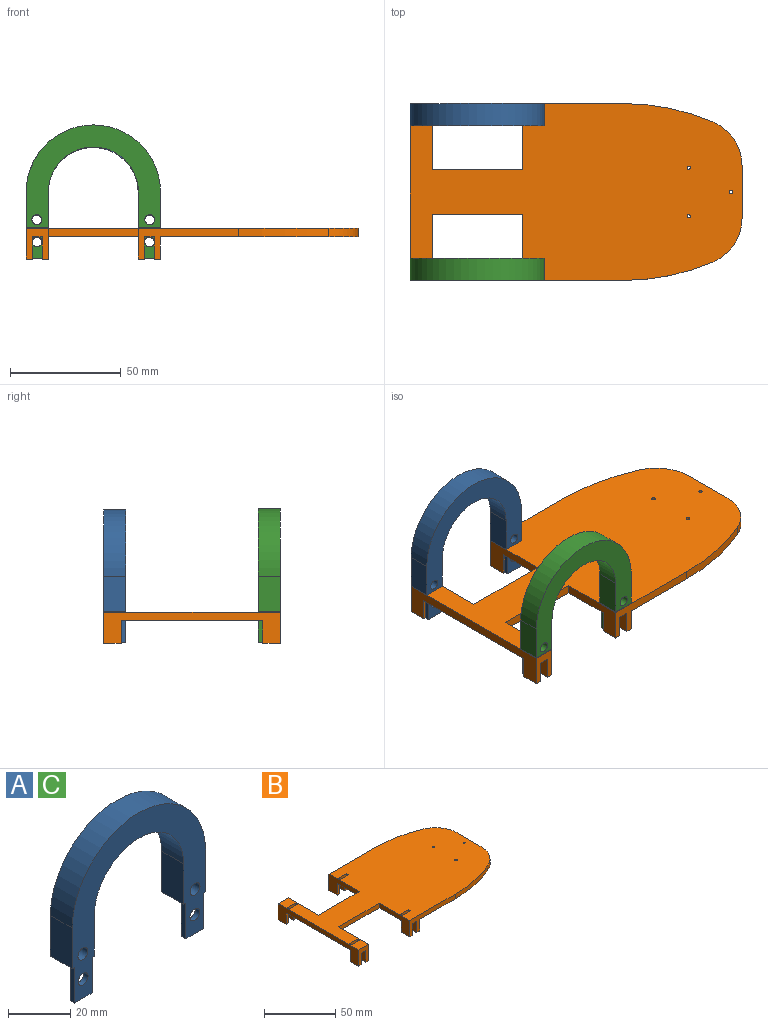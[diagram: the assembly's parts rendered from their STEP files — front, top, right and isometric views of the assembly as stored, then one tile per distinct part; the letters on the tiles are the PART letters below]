
ASSEMBLY  parts=3 mates=1
PART A: 22 faces, bbox 60.7x10x60.4 mm
  f0: plane 60.7x60.35mm, normal (0,-1,0), area 1276.8mm2, adj f2,f3,f4,f5,f6,f7,f8,f9
  f1: plane 60.7x46.35mm, normal (0,1,0), area 1084.6mm2, adj f2,f3,f4,f5,f6,f7,f8,f9
  f2: plane 10x10mm, normal (0,0,-1), area 84mm2, adj f0,f1,f5,f6,f14,f15,f16
  f3: plane 16x10mm, normal (1,0,0), area 160mm2, adj f0,f1,f4,f9
  f4: cylinder r=20.35mm len=40.7mm, axis (0,1,0), area 639.3mm2, adj f0,f1,f3,f5
  f5: plane 16x10mm, normal (-1,0,0), area 160mm2, adj f0,f1,f2,f4
  f6: plane 16x10mm, normal (1,0,0), area 160mm2, adj f0,f1,f2,f7
  f7: cylinder r=30.35mm len=60.7mm, axis (0,1,0), area 953.5mm2, adj f0,f1,f6,f8
  f8: plane 16x10mm, normal (-1,0,0), area 160mm2, adj f0,f1,f7,f9
  f9: plane 10x10mm, normal (0,0,-1), area 84mm2, adj f0,f1,f3,f8,f10,f11,f12
  f10: plane 14x2mm, normal (1,0,0), area 28mm2, adj f0,f9,f12,f13
  f11: plane 14x2mm, normal (-1,0,0), area 28mm2, adj f0,f9,f12,f13
  f12: plane 14x8mm, normal (0,1,0), area 96.1mm2, adj f9,f10,f11,f13,f19
  f13: plane 8x2mm, normal (0,0,-1), area 16mm2, adj f0,f10,f11,f12
  f14: plane 14x2mm, normal (-1,0,0), area 28mm2, adj f0,f2,f15,f17
  f15: plane 14x8mm, normal (0,1,0), area 96.1mm2, adj f2,f14,f16,f17,f18
  f16: plane 14x2mm, normal (1,0,0), area 28mm2, adj f0,f2,f15,f17
  f17: plane 8x2mm, normal (0,0,-1), area 16mm2, adj f0,f14,f15,f16
  f18: cylinder r=2.25mm len=4.5mm, axis (0,1,0), area 28.3mm2, adj f0,f15
  f19: cylinder r=2.25mm len=4.5mm, axis (0,1,0), area 28.3mm2, adj f0,f12
  f20: cylinder r=2.25mm len=10mm, axis (0,1,0), area 141.4mm2, adj f0,f1
  f21: cylinder r=2.25mm len=10mm, axis (0,1,0), area 141.4mm2, adj f0,f1
PART B: 59 faces, bbox 150x80x14 mm
  f0: plane 150x80mm, normal (0,0,-1), area 8584mm2, adj f6,f7,f8,f10,f12,f13,f14,f15
  f1: plane 150x80mm, normal (0,0,1), area 8904mm2, adj f6,f7,f8,f9,f10,f11,f12,f13
  f2: plane 8x4.5mm, normal (0,0,-1), area 36mm2, adj f7,f24,f48,f50
  f3: plane 8x4.5mm, normal (0,0,-1), area 36mm2, adj f9,f20,f43,f45
  f4: plane 8x4.5mm, normal (0,0,-1), area 36mm2, adj f8,f29,f38,f41
  f5: plane 8x4.5mm, normal (0,0,-1), area 36mm2, adj f11,f32,f34,f36
  f6: plane 23.72x4mm, normal (1,0,0), area 94.9mm2, adj f0,f1,f54,f55
  f7: plane 45.39x14mm, normal (0,1,0), area 236.6mm2, adj f0,f1,f2,f17,f47,f48,f49,f50
  f8: plane 45.39x14mm, normal (0,-1,0), area 236.6mm2, adj f0,f1,f4,f13,f38,f39,f40,f41
  f9: plane 14x10mm, normal (0,1,0), area 95mm2, adj f1,f3,f10,f15,f43,f44,f45,f46
  f10: plane 80x14mm, normal (-1,0,0), area 480mm2, adj f0,f1,f9,f11,f20,f32,f35,f44
  f11: plane 14x10mm, normal (0,-1,0), area 95mm2, adj f1,f5,f10,f12,f34,f35,f36,f37
  f12: plane 30x14mm, normal (1,0,0), area 200mm2, adj f0,f1,f11,f14,f32,f37
  f13: plane 30x14mm, normal (-1,0,0), area 200mm2, adj f0,f1,f8,f14,f29,f39
  f14: plane 40.7x4mm, normal (0,-1,0), area 162.8mm2, adj f0,f1,f12,f13
  f15: plane 30x14mm, normal (1,0,0), area 200mm2, adj f0,f1,f9,f16,f20,f46
  f16: plane 40.7x4mm, normal (0,1,0), area 162.8mm2, adj f0,f1,f15,f17
  f17: plane 30x14mm, normal (-1,0,0), area 200mm2, adj f0,f1,f7,f16,f24,f51
  f18: plane 8x4mm, normal (0,1,0), area 32mm2, adj f0,f1,f19,f21
  f19: plane 4x2mm, normal (-1,0,0), area 8mm2, adj f0,f1,f18,f20
  f20: plane 14x10mm, normal (0,-1,0), area 87mm2, adj f0,f1,f3,f10,f15,f19,f21,f43
  f21: plane 4x2mm, normal (1,0,0), area 8mm2, adj f0,f1,f18,f20
  f22: plane 8x4mm, normal (0,1,0), area 32mm2, adj f0,f1,f23,f25
  f23: plane 4x2mm, normal (-1,0,0), area 8mm2, adj f0,f1,f22,f24
  f24: plane 14x10mm, normal (0,-1,0), area 87mm2, adj f0,f1,f2,f17,f23,f25,f47,f48
  f25: plane 4x2mm, normal (1,0,0), area 8mm2, adj f0,f1,f22,f24
  f26: plane 4x2mm, normal (-1,0,0), area 8mm2, adj f0,f1,f27,f29
  f27: plane 8x4mm, normal (0,-1,0), area 32mm2, adj f0,f1,f26,f28
  f28: plane 4x2mm, normal (1,0,0), area 8mm2, adj f0,f1,f27,f29
  f29: plane 14x10mm, normal (0,1,0), area 87mm2, adj f0,f1,f4,f13,f26,f28,f38,f39
  f30: plane 8x4mm, normal (0,-1,0), area 32mm2, adj f0,f1,f31,f33
  f31: plane 4x2mm, normal (1,0,0), area 8mm2, adj f0,f1,f30,f32
  f32: plane 14x10mm, normal (0,1,0), area 87mm2, adj f0,f1,f5,f10,f12,f31,f33,f34
  f33: plane 4x2mm, normal (-1,0,0), area 8mm2, adj f0,f1,f30,f32
  f34: plane 10x8mm, normal (1,0,0), area 80mm2, adj f5,f11,f32,f35
  f35: plane 8x2.75mm, normal (0,0,-1), area 22mm2, adj f10,f11,f32,f34
  f36: plane 10x8mm, normal (-1,0,0), area 80mm2, adj f5,f11,f32,f37
  f37: plane 8x2.75mm, normal (0,0,-1), area 22mm2, adj f11,f12,f32,f36
  f38: plane 10x8mm, normal (1,0,0), area 80mm2, adj f4,f8,f29,f39
  f39: plane 8x2.75mm, normal (0,0,-1), area 22mm2, adj f8,f13,f29,f38
  f40: plane 10x8mm, normal (1,0,0), area 80mm2, adj f0,f8,f29,f42
  f41: plane 10x8mm, normal (-1,0,0), area 80mm2, adj f4,f8,f29,f42
  f42: plane 8x2.75mm, normal (0,0,-1), area 22mm2, adj f8,f29,f40,f41
  f43: plane 10x8mm, normal (1,0,0), area 80mm2, adj f3,f9,f20,f44
  f44: plane 8x2.75mm, normal (0,0,-1), area 22mm2, adj f9,f10,f20,f43
  f45: plane 10x8mm, normal (-1,0,0), area 80mm2, adj f3,f9,f20,f46
  f46: plane 8x2.75mm, normal (0,0,-1), area 22mm2, adj f9,f15,f20,f45
  f47: plane 10x8mm, normal (1,0,0), area 80mm2, adj f0,f7,f24,f49
  f48: plane 10x8mm, normal (-1,0,0), area 80mm2, adj f2,f7,f24,f49
  f49: plane 8x2.75mm, normal (0,0,-1), area 22mm2, adj f7,f24,f47,f48
  f50: plane 10x8mm, normal (1,0,0), area 80mm2, adj f2,f7,f24,f51
  f51: plane 8x2.75mm, normal (0,0,-1), area 22mm2, adj f7,f17,f24,f50
  f52: cylinder r=104.38mm len=40.77mm, axis (0,0,1), area 167.5mm2, adj f0,f1,f8,f54
  f53: cylinder r=104.38mm len=40.77mm, axis (0,0,1), area 167.5mm2, adj f0,f1,f7,f55
  f54: cylinder r=21.56mm len=19.85mm, axis (0,0,1), area 100.9mm2, adj f0,f1,f6,f52
  f55: cylinder r=21.56mm len=19.85mm, axis (0,0,1), area 100.9mm2, adj f0,f1,f6,f53
  f56: cylinder r=0.75mm len=4mm, axis (0,0,1), area 18.8mm2, adj f0,f1
  f57: cylinder r=0.75mm len=4mm, axis (0,0,1), area 18.8mm2, adj f0,f1
  f58: cylinder r=0.75mm len=4mm, axis (0,0,1), area 18.8mm2, adj f0,f1
PART C: same geometry as A
PLACE A t=(-68.85,44.94,21.59)mm
PLACE B t=(-24.1,5,1.52)mm fixed
PLACE C rot(axis=(0,0,1),180deg) t=(-68.75,-35,21.82)mm
MATE slider C.f17 <-> B.f0  axis (0,0,-1) through (-94.1,-25,-8.18)mm
